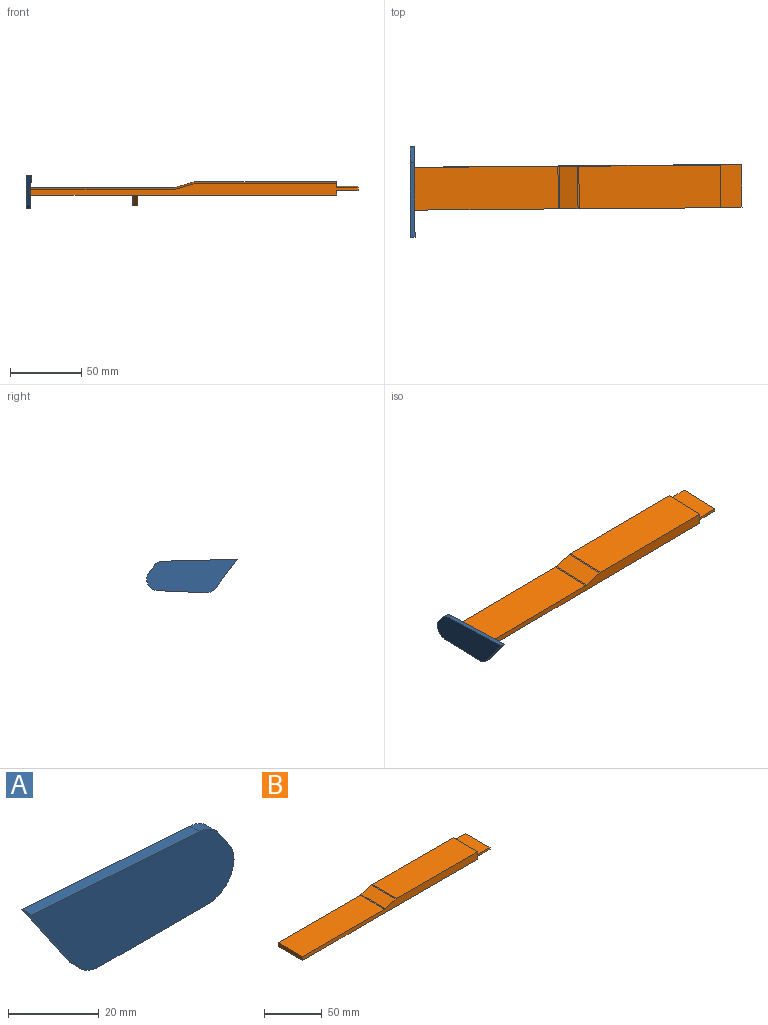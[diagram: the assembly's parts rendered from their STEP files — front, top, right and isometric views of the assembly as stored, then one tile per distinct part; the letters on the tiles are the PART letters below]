
ASSEMBLY  parts=2 mates=1
PART A: 9 faces, bbox 62.9x3x24.5 mm
  f0: plane 34x3mm, normal (0,0,-1), area 102mm2, adj f1,f6,f7,f8
  f1: cylinder r=8mm len=12.51mm, axis (0,1,0), area 52.1mm2, adj f0,f2,f7,f8
  f2: plane 4.85x3.31mm, normal (0.83,0,0.56), area 17.6mm2, adj f1,f3,f7,f8
  f3: cylinder r=8mm len=6.05mm, axis (0,1,0), area 21.7mm2, adj f2,f4,f7,f8
  f4: plane 52.17x3.62mm, normal (0.07,0,1), area 156.9mm2, adj f3,f5,f7,f8
  f5: plane 20.97x14.32mm, normal (-0.83,0,-0.56), area 76.2mm2, adj f4,f6,f7,f8
  f6: cylinder r=8mm len=6.61mm, axis (0,1,0), area 23.3mm2, adj f0,f5,f7,f8
  f7: plane 62.93x24.45mm, normal (0,-1,0), area 1144.8mm2, adj f0,f1,f2,f3,f4,f5,f6
  f8: plane 62.93x24.45mm, normal (0,1,0), area 1144.8mm2, adj f0,f1,f2,f3,f4,f5,f6
PART B: 25 faces, bbox 230x30x16 mm
  f0: plane 30x8mm, normal (-1,0,0), area 132.1mm2, adj f1,f3,f18,f19,f20,f21,f22,f23
  f1: plane 10x3mm, normal (0,0,-1), area 30mm2, adj f0,f2,f23,f24
  f2: plane 30x8mm, normal (1,0,0), area 132.1mm2, adj f1,f4,f18,f19,f20,f21,f22,f23
  f3: plane 72x30mm, normal (0,0,-1), area 2160mm2, adj f0,f9,f13,f14
  f4: plane 140x30mm, normal (0,0,-1), area 4200mm2, adj f2,f6,f13,f14
  f5: plane 30x3.05mm, normal (1,0,0), area 91.5mm2, adj f10,f13,f14,f15
  f6: plane 30x3.09mm, normal (1,0,0), area 92.1mm2, adj f4,f13,f14,f16
  f7: cylinder r=3mm len=30mm, axis (0,1,0), area 25.5mm2, adj f8,f12,f13,f14
  f8: plane 100.86x30mm, normal (0,0,1), area 3025.8mm2, adj f7,f9,f13,f14
  f9: plane 30x4mm, normal (-1,0,0), area 120mm2, adj f3,f8,f13,f14
  f10: plane 99.43x30mm, normal (0,0,1), area 2983mm2, adj f5,f11,f13,f14
  f11: cylinder r=3mm len=30mm, axis (0,1,0), area 25.5mm2, adj f10,f12,f13,f14
  f12: plane 30x13.03mm, normal (-0.28,0,0.96), area 407mm2, adj f7,f11,f13,f14
  f13: plane 230x8.04mm, normal (0,-1,0), area 1320.5mm2, adj f3,f4,f5,f6,f7,f8,f9,f10
  f14: plane 230x8.04mm, normal (0,1,0), area 1319.9mm2, adj f3,f4,f5,f6,f7,f8,f9,f10
  f15: plane 30x15mm, normal (0,0,1), area 450mm2, adj f5,f13,f14,f17
  f16: plane 30x15mm, normal (0,0,-1), area 450mm2, adj f6,f13,f14,f17
  f17: plane 30x1.94mm, normal (1,0,0), area 57.6mm2, adj f13,f14,f15,f16
  f18: cylinder r=4.75mm len=9.4mm, axis (-1,0,0), area 40.4mm2, adj f0,f2,f19,f21
  f19: plane 3x2mm, normal (0,0,1), area 6mm2, adj f0,f2,f18,f20
  f20: cylinder r=2.8mm len=5.4mm, axis (-1,0,0), area 21.9mm2, adj f0,f2,f19,f21
  f21: plane 3x2mm, normal (0,0,1), area 6mm2, adj f0,f2,f18,f20
  f22: cylinder r=1.55mm len=3.1mm, axis (-1,0,0), area 29.2mm2, adj f0,f2
  f23: plane 10x8mm, normal (0,-0.62,-0.78), area 38.4mm2, adj f0,f1,f2,f13
  f24: plane 10x8mm, normal (0,0.62,-0.78), area 38.4mm2, adj f0,f1,f2,f14
PLACE A rot(axis=(0.02,-0.02,1),90.5deg) t=(-96.96,72.24,0)mm
PLACE B rot(axis=(0.98,0,0.2),2.5deg) t=(18.25,85.83,-0.34)mm
MATE fastened B.f9 <-> A.f7  axis (-1,-0.01,0) through (-93.94,69.95,-3.02)mm
